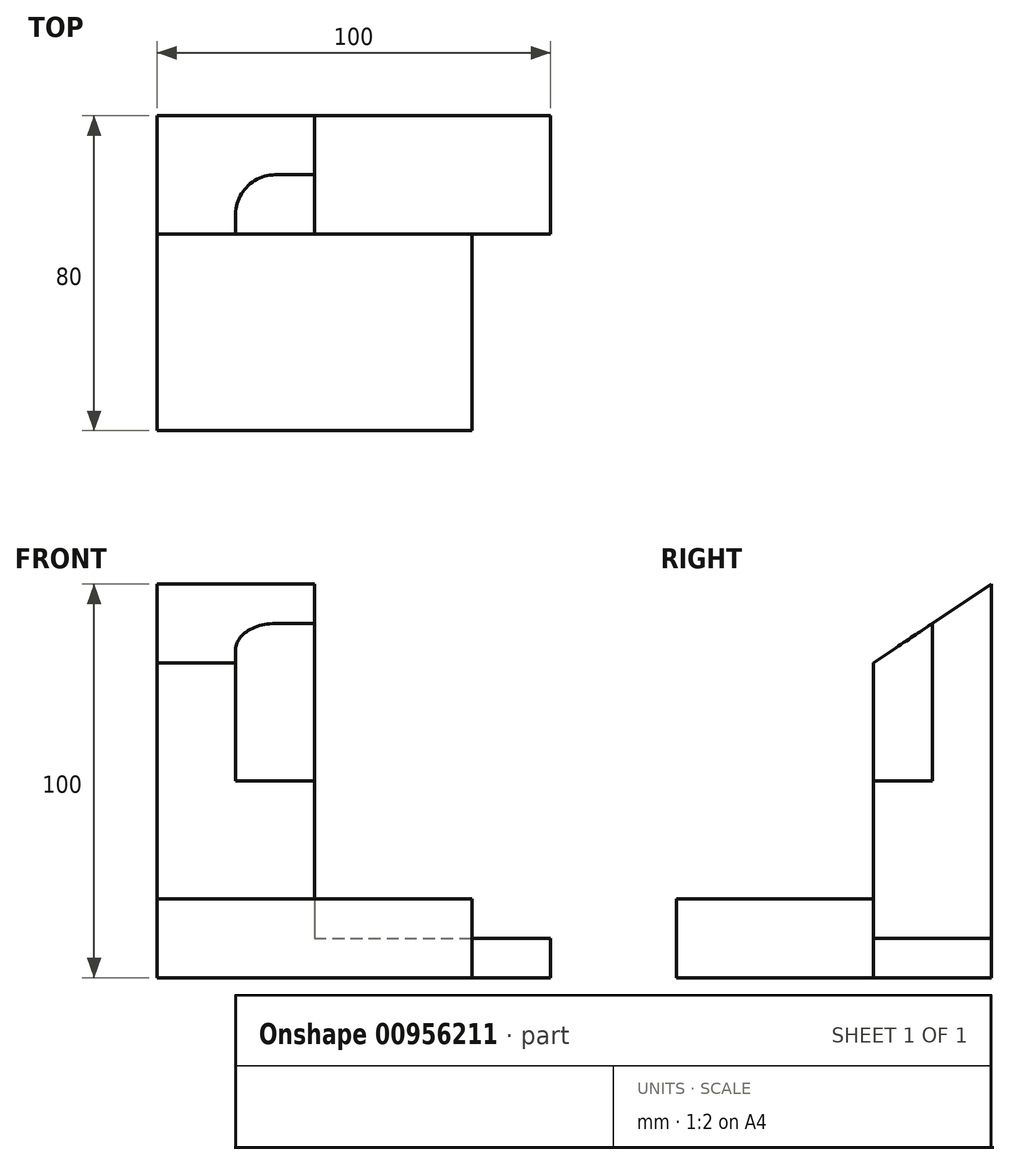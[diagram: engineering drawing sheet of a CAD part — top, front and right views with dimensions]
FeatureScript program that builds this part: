
annotation { "Feature Type Name" : "Feature", "Feature Type Description" : "" }
export const myFeature = defineFeature(function(context is Context, id is Id, definition is map)
    precondition{}
    {
        {
            var Q0;
            Q0=qCreatedBy(makeId("Top.planeOp"),FACE);
            var sketch = newSketch(context, id + "F0", { "sketchPlane" : qUnion([Q0])});
            skLineSegment(sketch, "E0.bottom", {"start": v(0, 0) * mm, "end": v(80, 0) * mm});
            skLineSegment(sketch, "E0.top", {"start": v(0, 50) * mm, "end": v(80, 50) * mm});
            skLineSegment(sketch, "E0.left", {"start": v(0, 0) * mm, "end": v(0, 50) * mm});
            skLineSegment(sketch, "E0.right", {"start": v(80, 0) * mm, "end": v(80, 50) * mm});
            skSolve(sketch);
        }
        {
            var Q0;
            Q0 = qSketchRegion(id + "F0", true);
            extrude(context, id + "F1", {"entities" : qUnion([Q0]), "depth" : 20 * mm, "offsetDistance" : 25 * mm});
        }
        {
            var Q0;
            Q0=qCreatedBy(makeId("Top.planeOp"),FACE);
            var sketch = newSketch(context, id + "F2", { "sketchPlane" : qUnion([Q0])});
            skLineSegment(sketch, "E1.bottom", {"start": v(0, 50) * mm, "end": v(100, 50) * mm});
            skLineSegment(sketch, "E1.top", {"start": v(0, 80) * mm, "end": v(100, 80) * mm});
            skLineSegment(sketch, "E1.left", {"start": v(0, 50) * mm, "end": v(0, 80) * mm});
            skLineSegment(sketch, "E1.right", {"start": v(100, 50) * mm, "end": v(100, 80) * mm});
            skSolve(sketch);
        }
        {
            var Q0;
            Q0 = qSketchRegion(id + "F2", true);
            extrude(context, id + "F3", {"entities" : qUnion([Q0]), "operationType" : NewBodyOperationType.ADD, "depth" : 10 * mm, "offsetDistance" : 25 * mm});
        }
        {
            var Q0;
            Q0=makeQuery(id+"F3.opExtrude","CAP_FACE",FACE,{"disambiguationData":[OSD([sQuery(id+"F2.wireOp",EDGE,"E1.bottom"),sQuery(id+"F2.wireOp",EDGE,"E1.top"),sQuery(id+"F2.wireOp",EDGE,"E1.left"),sQuery(id+"F2.wireOp",EDGE,"E1.right")])],"isStart":false});
            var sketch = newSketch(context, id + "F4", { "sketchPlane" : qUnion([Q0])});
            skLineSegment(sketch, "E2.bottom", {"start": v(0, 80) * mm, "end": v(40, 80) * mm});
            skLineSegment(sketch, "E2.top", {"start": v(0, 50) * mm, "end": v(40, 50) * mm});
            skLineSegment(sketch, "E2.left", {"start": v(0, 80) * mm, "end": v(0, 50) * mm});
            skLineSegment(sketch, "E2.right", {"start": v(40, 80) * mm, "end": v(40, 50) * mm});
            skSolve(sketch);
        }
        {
            var Q0;
            Q0 = qSketchRegion(id + "F4", true);
            extrude(context, id + "F5", {"entities" : qUnion([Q0]), "operationType" : NewBodyOperationType.ADD, "depth" : 90 * mm, "offsetDistance" : 25 * mm});
        }
        {
            var Q0;
            Q0=makeQuery(id+"F5.opExtrude","CAP_EDGE",EDGE,{"disambiguationData":[OSD([sQuery(id+"F4.wireOp",EDGE,"E2.top")])],"isStart":false});
            chamfer(context, id + "F6", {"entities" : qUnion([Q0]), "chamferType" : ChamferType.TWO_OFFSETS, "width1" : 30 * mm, "oppositeDirection" : false, "width2" : 20 * mm, "tangentPropagation" : true});
        }
        {
            var Q0;
            Q0=makeQuery(id+"F3.boolean.opBoolean","MERGE",FACE,{"derivedFrom":[makeQuery(id+"F1.opExtrude","CAP_FACE",FACE,{"disambiguationData":[OSD([sQuery(id+"F0.wireOp",EDGE,"E0.bottom"),sQuery(id+"F0.wireOp",EDGE,"E0.top"),sQuery(id+"F0.wireOp",EDGE,"E0.left"),sQuery(id+"F0.wireOp",EDGE,"E0.right")])],"isStart":true}),makeQuery(id+"F3.opExtrude","CAP_FACE",FACE,{"disambiguationData":[OSD([sQuery(id+"F2.wireOp",EDGE,"E1.bottom"),sQuery(id+"F2.wireOp",EDGE,"E1.top"),sQuery(id+"F2.wireOp",EDGE,"E1.left"),sQuery(id+"F2.wireOp",EDGE,"E1.right")])],"isStart":true})]});
            cPlane(context, id + "F7", {"entities" : qUnion([Q0]), "cplaneType" : CPlaneType.OFFSET, "offset" : 50 * mm, "oppositeDirection" : true, "width" : 150 * mm, "height" : 150 * mm});
        }
        {
            var Q0;
            Q0=qCreatedBy(id+"F7.planeOp",FACE);
            var sketch = newSketch(context, id + "F8", { "sketchPlane" : qUnion([Q0])});
            skLineSegment(sketch, "E3", {"start": v(40, -65) * mm, "end": v(40, -50) * mm});
            skLineSegment(sketch, "E4", {"start": v(40, -50) * mm, "end": v(20, -50) * mm});
            skLineSegment(sketch, "E5", {"start": v(20, -50) * mm, "end": v(20, -55) * mm});
            skLineSegment(sketch, "E6", {"start": v(30, -65) * mm, "end": v(40, -65) * mm});
            skPoint(sketch, "E7.visualSharp", {"position": v(20, -65) * mm});
            skArc(sketch, "E7.filletArc", {"start": v(20, -55) * mm, "mid": v(22.93, -62.07) * mm, "end": v(30, -65) * mm});
            skSolve(sketch);
        }
        {
            var Q0;
            Q0 = qSketchRegion(id + "F8", true);
            extrude(context, id + "F9", {"entities" : qUnion([Q0]), "operationType" : NewBodyOperationType.REMOVE, "endBound" : BoundingType.THROUGH_ALL, "oppositeDirection" : true, "depth" : 25 * mm, "offsetDistance" : 25 * mm});
        }
    });
